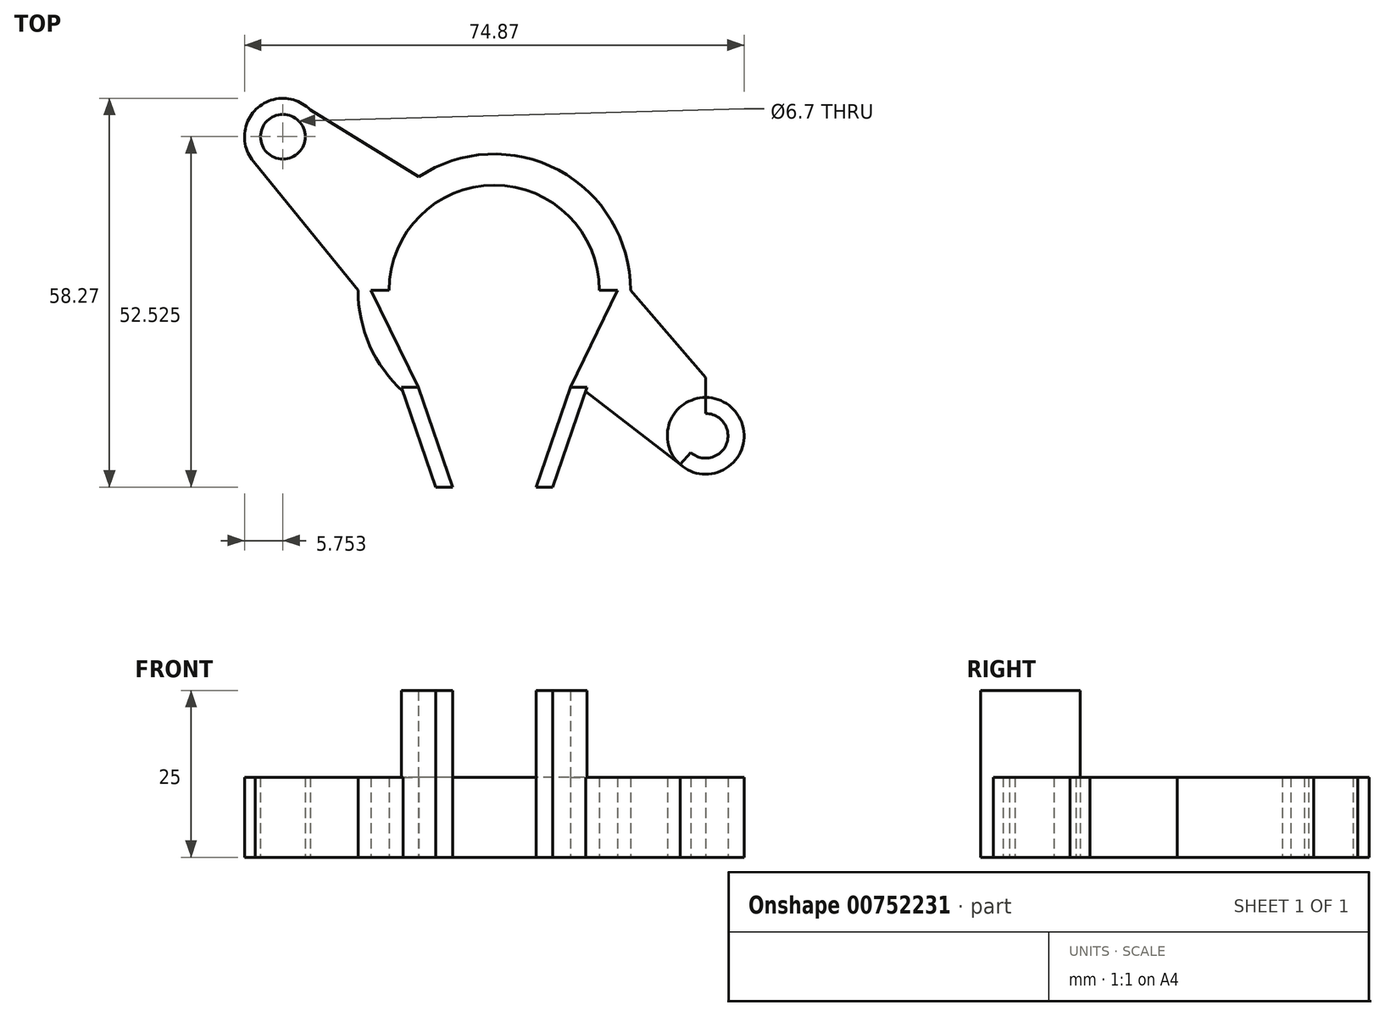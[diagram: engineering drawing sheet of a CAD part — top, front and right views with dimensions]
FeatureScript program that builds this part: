
annotation { "Feature Type Name" : "Feature", "Feature Type Description" : "" }
export const myFeature = defineFeature(function(context is Context, id is Id, definition is map)
    precondition{}
    {
        {
            var Q0;
            Q0=qCreatedBy(makeId("Top.planeOp"),FACE);
            var sketch = newSketch(context, id + "F0", { "sketchPlane" : qUnion([Q0])});
            skLineSegment(sketch, "E0.bottom", {"start": v(-52.47, 38.18) * mm, "end": v(4.2, 38.18) * mm});
            skLineSegment(sketch, "E0.left", {"start": v(-55.82, 34.83) * mm, "end": v(-55.82, -4.47) * mm});
            skLineSegment(sketch, "E0.right", {"start": v(7.55, 34.83) * mm, "end": v(7.55, -3.3) * mm});
            skCircle(sketch, "E1", {"center": v(7.55, 38.18) * mm, "radius": 3.35 * mm});
            skCircle(sketch, "E2", {"center": v(-55.82, 38.18) * mm, "radius": 3.35 * mm});
            skCircle(sketch, "E3", {"center": v(-55.82, -7.82) * mm, "radius": 3.35 * mm});
            skCircle(sketch, "E4", {"center": v(7.55, -6.66) * mm, "radius": 3.35 * mm});
            skCircle(sketch, "E5", {"center": v(-55.82, 38.18) * mm, "radius": 5.75 * mm});
            skCircle(sketch, "E6", {"center": v(7.55, 38.18) * mm, "radius": 5.75 * mm});
            skCircle(sketch, "E7", {"center": v(7.55, -6.66) * mm, "radius": 5.75 * mm});
            skCircle(sketch, "E8", {"center": v(-55.82, -7.82) * mm, "radius": 5.75 * mm});
            skPoint(sketch, "E9.first.point", {"position": v(-24.13, 38.18) * mm});
            skPoint(sketch, "E9.second.point", {"position": v(-55.82, 15.18) * mm});
            skPoint(sketch, "E10.middle", {"position": v(-24.13, 15.17) * mm});
            skCircle(sketch, "E11", {"center": v(-24.13, 15.17) * mm, "radius": 15.75 * mm});
            skLineSegment(sketch, "E12", {"start": v(-24.13, -7.82) * mm, "end": v(-24.13, -7.85) * mm});
            skLineSegment(sketch, "E13", {"start": v(-35.53, 0.6) * mm, "end": v(-30.38, -14.34) * mm});
            skLineSegment(sketch, "E14", {"start": v(-17.88, -14.34) * mm, "end": v(-12.74, 0.6) * mm});
            skLineSegment(sketch, "E15", {"start": v(-30.38, -14.34) * mm, "end": v(-32.88, -14.34) * mm});
            skLineSegment(sketch, "E16", {"start": v(-32.88, -14.34) * mm, "end": v(-38.03, 0.64) * mm});
            skLineSegment(sketch, "E17", {"start": v(-38.03, 0.64) * mm, "end": v(-35.53, 0.6) * mm});
            skLineSegment(sketch, "E18", {"start": v(-17.88, -14.34) * mm, "end": v(-15.38, -14.34) * mm});
            skLineSegment(sketch, "E19", {"start": v(-15.38, -14.34) * mm, "end": v(-10.24, 0.6) * mm});
            skLineSegment(sketch, "E20", {"start": v(-10.24, 0.6) * mm, "end": v(-12.74, 0.6) * mm});
            skLineSegment(sketch, "E21.trimOffspring", {"start": v(-55.82, -7.82) * mm, "end": v(-55.82, -7.85) * mm});
            skLineSegment(sketch, "E22.trimOffspring", {"start": v(7.55, 38.18) * mm, "end": v(7.55, 38.18) * mm});
            skPoint(sketch, "E23.orphan", {"position": v(-24.13, -14.34) * mm});
            skLineSegment(sketch, "E24", {"start": v(-24.13, 15.17) * mm, "end": v(-42.63, 15.17) * mm});
            skLineSegment(sketch, "E25", {"start": v(-35.53, 0.6) * mm, "end": v(-42.63, 15.17) * mm});
            skLineSegment(sketch, "E26", {"start": v(-24.13, 15.17) * mm, "end": v(-5.63, 15.17) * mm});
            skLineSegment(sketch, "E27", {"start": v(-12.74, 0.6) * mm, "end": v(-5.63, 15.17) * mm});
            skLineSegment(sketch, "E28", {"start": v(-30.38, -14.34) * mm, "end": v(-17.88, -14.34) * mm});
            skLineSegment(sketch, "E29", {"start": v(-42.63, 15.17) * mm, "end": v(-55.82, 15.18) * mm});
            skLineSegment(sketch, "E30", {"start": v(-5.63, 15.17) * mm, "end": v(7.55, 15.17) * mm});
            skLineSegment(sketch, "E31", {"start": v(-24.13, 15.17) * mm, "end": v(-24.13, -14.34) * mm});
            skLineSegment(sketch, "E32", {"start": v(-24.13, 15.17) * mm, "end": v(-24.13, 38.18) * mm});
            skLineSegment(sketch, "E33", {"start": v(-35.53, 0.6) * mm, "end": v(-12.74, 0.6) * mm});
            skLineSegment(sketch, "E34", {"start": v(-24.13, -7.82) * mm, "end": v(1.92, -7.82) * mm});
            skLineSegment(sketch, "E35", {"start": v(-24.13, -7.82) * mm, "end": v(-50.07, -7.82) * mm});
            skLineSegment(sketch, "E36", {"start": v(7.55, -6.66) * mm, "end": v(11.38, -2.37) * mm});
            skLineSegment(sketch, "E37", {"start": v(11.38, -2.37) * mm, "end": v(7.55, -6.66) * mm});
            skLineSegment(sketch, "E38", {"start": v(7.55, -6.66) * mm, "end": v(3.72, -10.95) * mm});
            skLineSegment(sketch, "E39", {"start": v(-55.82, 38.18) * mm, "end": v(-59.94, 34.18) * mm});
            skLineSegment(sketch, "E40", {"start": v(-55.82, 38.18) * mm, "end": v(-51.7, 42.2) * mm});
            skArc(sketch, "E41", {"start": v(-3.71, 15.17) * mm, "mid": v(-32.43, 33.82) * mm, "end": v(-37.8, 0) * mm});
            skLineSegment(sketch, "E42", {"start": v(11.38, -2.37) * mm, "end": v(-3.71, 15.17) * mm});
            skLineSegment(sketch, "E43", {"start": v(-51.7, 42.2) * mm, "end": v(-35.46, 32.16) * mm});
            skLineSegment(sketch, "E44", {"start": v(-59.94, 34.18) * mm, "end": v(-44.55, 15.17) * mm});
            skPoint(sketch, "E45.trimOffspring.end.orphan", {"position": v(-10.24, 0.2) * mm});
            skLineSegment(sketch, "E46", {"start": v(3.72, -10.95) * mm, "end": v(-10.44, 0) * mm});
            skSolve(sketch);
        }
        {
            var Q0;
            {var subQ7=sQuery(id+"F0.wireOp",EDGE,"E5");var subQ9=sQuery(id+"F0.wireOp",EDGE,"E0.bottom");var subQ11=makeQuery(id+"F0.imprint","INTERSECT",VERTEX,{"derivedFrom":[subQ7,subQ9]});Q0=makeQuery(id+"F0.imprint","IMPRINT",FACE,{"disambiguationData":[TD([[makeQuery(id+"F0.imprint","IMPRINT",EDGE,{"disambiguationData":[TD([[subQ11,1.0]])],"derivedFrom":subQ7}),-1.0]])]});}
            var Q1;
            {var subQ0=sQuery(id+"F0.wireOp",EDGE,"E0.bottom");var subQ1=sQuery(id+"F0.wireOp",EDGE,"E2");var subQ2=makeQuery(id+"F0.imprint","INTERSECT",VERTEX,{"derivedFrom":[subQ1,subQ0]});Q1=makeQuery(id+"F0.imprint","IMPRINT",FACE,{"disambiguationData":[TD([[makeQuery(id+"F0.imprint","IMPRINT",EDGE,{"disambiguationData":[TD([[subQ2,1.0]])],"derivedFrom":subQ1}),-1.0]])]});}
            var Q2;
            {var subQ0=sQuery(id+"F0.wireOp",EDGE,"E44");var subQ3=sQuery(id+"F0.wireOp",EDGE,"E0.left");var subQ5=makeQuery(id+"F0.imprint","INTERSECT",VERTEX,{"derivedFrom":[subQ3,subQ0]});Q2=makeQuery(id+"F0.imprint","IMPRINT",FACE,{"disambiguationData":[TD([[makeQuery(id+"F0.imprint","IMPRINT",EDGE,{"disambiguationData":[TD([[subQ5,1.0]])],"derivedFrom":subQ3}),-1.0]])]});}
            var Q3;
            {var subQ0=sQuery(id+"F0.wireOp",EDGE,"E0.left");var subQ1=sQuery(id+"F0.wireOp",EDGE,"E2");var subQ2=makeQuery(id+"F0.imprint","INTERSECT",VERTEX,{"derivedFrom":[subQ1,subQ0]});Q3=makeQuery(id+"F0.imprint","IMPRINT",FACE,{"disambiguationData":[TD([[makeQuery(id+"F0.imprint","IMPRINT",EDGE,{"disambiguationData":[TD([[subQ2,1.0]])],"derivedFrom":subQ1}),-1.0]])]});}
            var Q4;
            {var subQ0=sQuery(id+"F0.wireOp",EDGE,"E40");var subQ1=sQuery(id+"F0.wireOp",EDGE,"E2");var subQ2=makeQuery(id+"F0.imprint","INTERSECT",VERTEX,{"derivedFrom":[subQ1,subQ0]});Q4=makeQuery(id+"F0.imprint","IMPRINT",FACE,{"disambiguationData":[TD([[makeQuery(id+"F0.imprint","IMPRINT",EDGE,{"disambiguationData":[TD([[subQ2,-1.0]])],"derivedFrom":subQ1}),-1.0]])]});}
            var Q5;
            {var subQ0=sQuery(id+"F0.wireOp",EDGE,"E0.bottom");var subQ1=sQuery(id+"F0.wireOp",EDGE,"E2");var subQ2=makeQuery(id+"F0.imprint","INTERSECT",VERTEX,{"derivedFrom":[subQ1,subQ0]});Q5=makeQuery(id+"F0.imprint","IMPRINT",FACE,{"disambiguationData":[TD([[makeQuery(id+"F0.imprint","IMPRINT",EDGE,{"disambiguationData":[TD([[subQ2,-1.0]])],"derivedFrom":subQ1}),-1.0]])]});}
            var Q6;
            {var subQ0=sQuery(id+"F0.wireOp",EDGE,"E43");var subQ3=sQuery(id+"F0.wireOp",EDGE,"E0.bottom");var subQ5=makeQuery(id+"F0.imprint","INTERSECT",VERTEX,{"derivedFrom":[subQ3,subQ0]});Q6=makeQuery(id+"F0.imprint","IMPRINT",FACE,{"disambiguationData":[TD([[makeQuery(id+"F0.imprint","IMPRINT",EDGE,{"disambiguationData":[TD([[subQ5,1.0]])],"derivedFrom":subQ3}),1.0]])]});}
            var Q7;
            {var subQ0=sQuery(id+"F0.wireOp",EDGE,"E32");var subQ1=sQuery(id+"F0.wireOp",EDGE,"E11");var subQ2=makeQuery(id+"F0.imprint","INTERSECT",VERTEX,{"derivedFrom":[subQ1,subQ0]});Q7=makeQuery(id+"F0.imprint","IMPRINT",FACE,{"disambiguationData":[TD([[makeQuery(id+"F0.imprint","IMPRINT",EDGE,{"disambiguationData":[TD([[subQ2,-1.0]])],"derivedFrom":subQ1}),-1.0]])]});}
            var Q8;
            {var subQ0=sQuery(id+"F0.wireOp",EDGE,"E32");var subQ1=sQuery(id+"F0.wireOp",EDGE,"E11");var subQ2=makeQuery(id+"F0.imprint","INTERSECT",VERTEX,{"derivedFrom":[subQ1,subQ0]});Q8=makeQuery(id+"F0.imprint","IMPRINT",FACE,{"disambiguationData":[TD([[makeQuery(id+"F0.imprint","IMPRINT",EDGE,{"disambiguationData":[TD([[subQ2,1.0]])],"derivedFrom":subQ1}),-1.0]])]});}
            var Q9;
            {var subQ1=sQuery(id+"F0.wireOp",EDGE,"E17");Q9=makeQuery(id+"F0.imprint","IMPRINT",FACE,{"disambiguationData":[TD([[makeQuery(id+"F0.imprint","IMPRINT",EDGE,{"derivedFrom":subQ1}),1.0]])]});}
            var Q10;
            {var subQ0=sQuery(id+"F0.wireOp",EDGE,"E17");Q10=makeQuery(id+"F0.imprint","IMPRINT",FACE,{"disambiguationData":[TD([[makeQuery(id+"F0.imprint","IMPRINT",EDGE,{"derivedFrom":subQ0}),-1.0]])]});}
            var Q11;
            {var subQ0=sQuery(id+"F0.wireOp",EDGE,"E15");Q11=makeQuery(id+"F0.imprint","IMPRINT",FACE,{"disambiguationData":[TD([[makeQuery(id+"F0.imprint","IMPRINT",EDGE,{"derivedFrom":subQ0}),-1.0]])]});}
            var Q12;
            {var subQ0=sQuery(id+"F0.wireOp",EDGE,"E18");Q12=makeQuery(id+"F0.imprint","IMPRINT",FACE,{"disambiguationData":[TD([[makeQuery(id+"F0.imprint","IMPRINT",EDGE,{"derivedFrom":subQ0}),1.0]])]});}
            var Q13;
            {var subQ0=sQuery(id+"F0.wireOp",EDGE,"E20");Q13=makeQuery(id+"F0.imprint","IMPRINT",FACE,{"disambiguationData":[TD([[makeQuery(id+"F0.imprint","IMPRINT",EDGE,{"derivedFrom":subQ0}),1.0]])]});}
            var Q14;
            {var subQ0=sQuery(id+"F0.wireOp",EDGE,"E20");Q14=makeQuery(id+"F0.imprint","IMPRINT",FACE,{"disambiguationData":[TD([[makeQuery(id+"F0.imprint","IMPRINT",EDGE,{"derivedFrom":subQ0}),-1.0]])]});}
            var Q15;
            {var subQ0=sQuery(id+"F0.wireOp",EDGE,"E37");var subQ1=sQuery(id+"F0.wireOp",EDGE,"E4");var subQ2=makeQuery(id+"F0.imprint","INTERSECT",VERTEX,{"derivedFrom":[subQ1,subQ0]});Q15=makeQuery(id+"F0.imprint","IMPRINT",FACE,{"disambiguationData":[TD([[makeQuery(id+"F0.imprint","IMPRINT",EDGE,{"disambiguationData":[TD([[subQ2,1.0]])],"derivedFrom":subQ1}),-1.0]])]});}
            var Q16;
            {var subQ0=sQuery(id+"F0.wireOp",EDGE,"E0.right");var subQ1=sQuery(id+"F0.wireOp",EDGE,"E4");var subQ2=makeQuery(id+"F0.imprint","INTERSECT",VERTEX,{"derivedFrom":[subQ1,subQ0]});Q16=makeQuery(id+"F0.imprint","IMPRINT",FACE,{"disambiguationData":[TD([[makeQuery(id+"F0.imprint","IMPRINT",EDGE,{"disambiguationData":[TD([[subQ2,1.0]])],"derivedFrom":subQ1}),-1.0]])]});}
            var Q17;
            {var subQ0=sQuery(id+"F0.wireOp",EDGE,"E0.right");var subQ1=sQuery(id+"F0.wireOp",EDGE,"E4");var subQ2=makeQuery(id+"F0.imprint","INTERSECT",VERTEX,{"derivedFrom":[subQ1,subQ0]});Q17=makeQuery(id+"F0.imprint","IMPRINT",FACE,{"disambiguationData":[TD([[makeQuery(id+"F0.imprint","IMPRINT",EDGE,{"disambiguationData":[TD([[subQ2,-1.0]])],"derivedFrom":subQ1}),-1.0]])]});}
            var Q18;
            {var subQ0=sQuery(id+"F0.wireOp",EDGE,"E34");var subQ1=sQuery(id+"F0.wireOp",EDGE,"E7");var subQ2=makeQuery(id+"F0.imprint","INTERSECT",VERTEX,{"derivedFrom":[subQ1,subQ0]});Q18=makeQuery(id+"F0.imprint","IMPRINT",FACE,{"disambiguationData":[TD([[makeQuery(id+"F0.imprint","IMPRINT",EDGE,{"disambiguationData":[TD([[subQ2,1.0]])],"derivedFrom":subQ0}),-1.0]])]});}
            var Q19;
            {var subQ0=sQuery(id+"F0.wireOp",EDGE,"E42");var subQ3=sQuery(id+"F0.wireOp",EDGE,"E0.right");var subQ5=makeQuery(id+"F0.imprint","INTERSECT",VERTEX,{"derivedFrom":[subQ3,subQ0]});Q19=makeQuery(id+"F0.imprint","IMPRINT",FACE,{"disambiguationData":[TD([[makeQuery(id+"F0.imprint","IMPRINT",EDGE,{"disambiguationData":[TD([[subQ5,-1.0]])],"derivedFrom":subQ3}),1.0]])]});}
            extrude(context, id + "F1", {"entities" : qUnion([Q0, Q1, Q2, Q3, Q4, Q5, Q6, Q7, Q8, Q9, Q10, Q11, Q12, Q13, Q14, Q15, Q16, Q17, Q18, Q19]), "depth" : 12 * mm, "offsetDistance" : 25 * mm});
        }
        {
            var Q0;
            {var subQ0=sQuery(id+"F0.wireOp",EDGE,"E17");Q0=makeQuery(id+"F0.imprint","IMPRINT",FACE,{"disambiguationData":[TD([[makeQuery(id+"F0.imprint","IMPRINT",EDGE,{"derivedFrom":subQ0}),-1.0]])]});}
            var Q1;
            {var subQ0=sQuery(id+"F0.wireOp",EDGE,"E15");Q1=makeQuery(id+"F0.imprint","IMPRINT",FACE,{"disambiguationData":[TD([[makeQuery(id+"F0.imprint","IMPRINT",EDGE,{"derivedFrom":subQ0}),-1.0]])]});}
            var Q2;
            {var subQ0=sQuery(id+"F0.wireOp",EDGE,"E18");Q2=makeQuery(id+"F0.imprint","IMPRINT",FACE,{"disambiguationData":[TD([[makeQuery(id+"F0.imprint","IMPRINT",EDGE,{"derivedFrom":subQ0}),1.0]])]});}
            var Q3;
            {var subQ0=sQuery(id+"F0.wireOp",EDGE,"E20");Q3=makeQuery(id+"F0.imprint","IMPRINT",FACE,{"disambiguationData":[TD([[makeQuery(id+"F0.imprint","IMPRINT",EDGE,{"derivedFrom":subQ0}),1.0]])]});}
            extrude(context, id + "F2", {"entities" : qUnion([Q0, Q1, Q2, Q3]), "operationType" : NewBodyOperationType.ADD, "depth" : 25 * mm, "offsetDistance" : 25 * mm});
        }
    });
